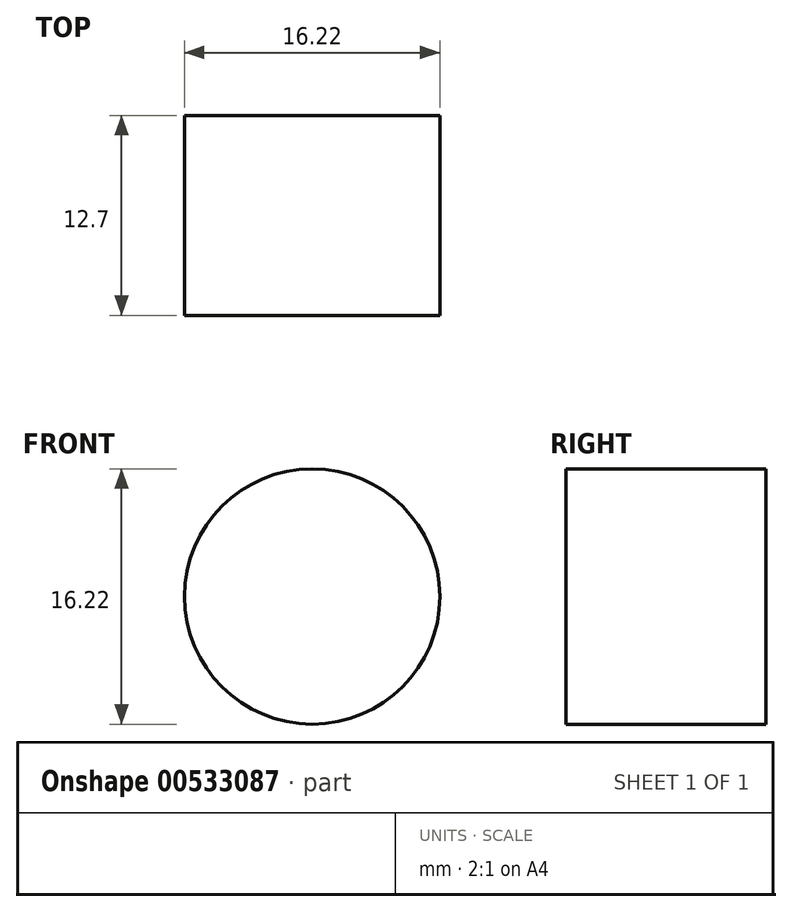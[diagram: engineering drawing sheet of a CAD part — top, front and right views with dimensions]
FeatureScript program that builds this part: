
annotation { "Feature Type Name" : "Feature", "Feature Type Description" : "" }
export const myFeature = defineFeature(function(context is Context, id is Id, definition is map)
    precondition{}
    {
        {
            var Q0;
            Q0=qCreatedBy(makeId("Front.planeOp"),FACE);
            var sketch = newSketch(context, id + "F0", { "sketchPlane" : qUnion([Q0])});
            skLineSegment(sketch, "E0.bottom", {"start": v(-55.08, 37.38) * mm, "end": v(60.6, 37.38) * mm});
            skLineSegment(sketch, "E0.top", {"start": v(-55.08, -37.38) * mm, "end": v(60.6, -37.38) * mm});
            skLineSegment(sketch, "E0.left", {"start": v(-55.08, 37.38) * mm, "end": v(-55.08, -37.38) * mm});
            skLineSegment(sketch, "E0.right", {"start": v(60.6, 37.38) * mm, "end": v(60.6, -37.38) * mm});
            skPoint(sketch, "E0.middle", {"position": v(2.75, 0) * mm});
            skSolve(sketch);
        }
        {
            var Q0;
            Q0=makeQuery(id+"F0.imprint","IMPRINT",FACE,{"disambiguationData":[TD([[makeQuery(id+"F0.imprint","IMPRINT",EDGE,{"derivedFrom":sQuery(id+"F0.wireOp",EDGE,"E0.bottom")}),-1.0]])]});
            extrude(context, id + "F1", {"entities" : qUnion([Q0]), "endBound" : BoundingType.SYMMETRIC, "depth" : 25.4 * mm, "offsetDistance" : 25.4 * mm});
        }
        {
            var Q0;
            Q0=makeQuery(id+"F1.opExtrude","CAP_FACE",FACE,{"disambiguationData":[OSD([sQuery(id+"F0.wireOp",EDGE,"E0.bottom"),sQuery(id+"F0.wireOp",EDGE,"E0.top"),sQuery(id+"F0.wireOp",EDGE,"E0.left"),sQuery(id+"F0.wireOp",EDGE,"E0.right")])],"isStart":false});
            var sketch = newSketch(context, id + "F2", { "sketchPlane" : qUnion([Q0])});
            skCircle(sketch, "E1", {"center": v(-30.3, 18.1) * mm, "radius": 9.46 * mm});
            skSolve(sketch);
        }
        {
            var Q0;
            Q0=makeQuery(id+"F2.imprint","IMPRINT",FACE,{"disambiguationData":[TD([[makeQuery(id+"F2.imprint","IMPRINT",EDGE,{"derivedFrom":sQuery(id+"F2.wireOp",EDGE,"E1")}),1.0]])]});
            extrude(context, id + "F3", {"entities" : qUnion([Q0]), "operationType" : NewBodyOperationType.ADD, "oppositeDirection" : true, "depth" : 25.4 * mm, "offsetDistance" : 25.4 * mm});
        }
        {
            var Q0;
            Q0=makeQuery(id+"F1.opExtrude","CAP_FACE",FACE,{"disambiguationData":[OSD([sQuery(id+"F0.wireOp",EDGE,"E0.bottom"),sQuery(id+"F0.wireOp",EDGE,"E0.top"),sQuery(id+"F0.wireOp",EDGE,"E0.left"),sQuery(id+"F0.wireOp",EDGE,"E0.right")])],"isStart":true});
            var sketch = newSketch(context, id + "F4", { "sketchPlane" : qUnion([Q0])});
            skCircle(sketch, "E2", {"center": v(-43.97, 24.52) * mm, "radius": 8.49 * mm});
            skSolve(sketch);
        }
        {
            var Q0;
            Q0 = qSketchRegion(id + "F4", true);
            var Q1;
            Q1=makeQuery(id+"F4.imprint","IMPRINT",FACE,{"disambiguationData":[TD([[makeQuery(id+"F4.imprint","IMPRINT",EDGE,{"derivedFrom":sQuery(id+"F4.wireOp",EDGE,"E2")}),-1.0]])]});
            extrude(context, id + "F5", {"entities" : qUnion([Q0, Q1]), "operationType" : NewBodyOperationType.ADD, "oppositeDirection" : true, "depth" : 25.4 * mm, "offsetDistance" : 25.4 * mm});
        }
        {
            var Q0;
            Q0=qCreatedBy(makeId("Front.planeOp"),FACE);
            var sketch = newSketch(context, id + "F6", { "sketchPlane" : qUnion([Q0])});
            skCircle(sketch, "E3", {"center": v(37.15, 23.07) * mm, "radius": 8.11 * mm});
            skSolve(sketch);
        }
        {
            var Q0;
            Q0 = qSketchRegion(id + "F6", true);
            var Q1;
            Q1=makeQuery(id+"F1.opExtrude","CAP_FACE",FACE,{"disambiguationData":[OSD([sQuery(id+"F0.wireOp",EDGE,"E0.bottom"),sQuery(id+"F0.wireOp",EDGE,"E0.top"),sQuery(id+"F0.wireOp",EDGE,"E0.left"),sQuery(id+"F0.wireOp",EDGE,"E0.right")])],"isStart":true});
            extrude(context, id + "F7", {"entities" : qUnion([Q0, Q1]), "operationType" : NewBodyOperationType.INTERSECT, "oppositeDirection" : true, "depth" : 25.4 * mm, "offsetDistance" : 25.4 * mm});
        }
    });
